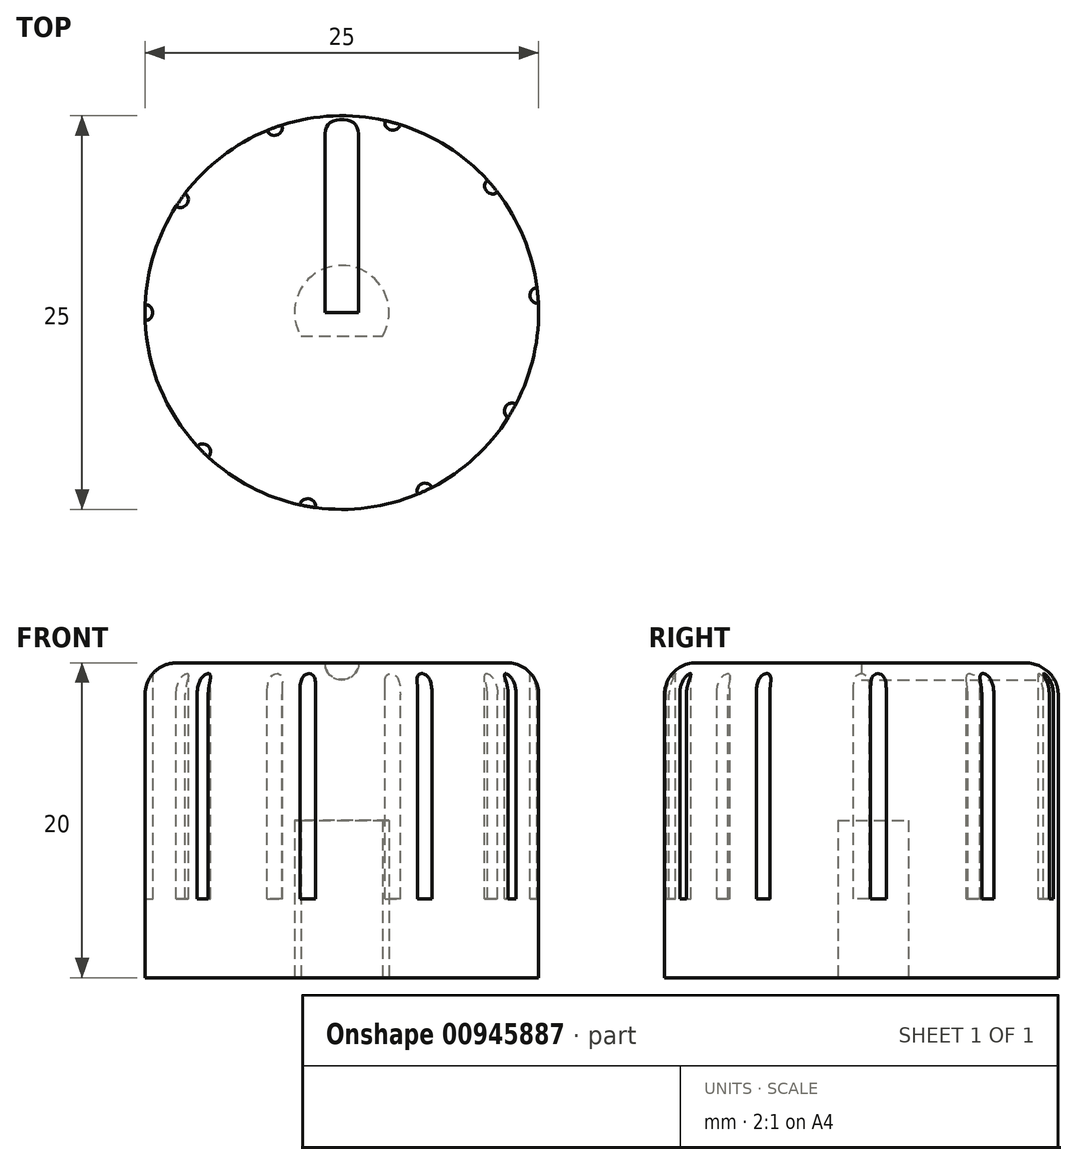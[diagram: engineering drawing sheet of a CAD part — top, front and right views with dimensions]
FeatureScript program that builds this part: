
annotation { "Feature Type Name" : "Feature", "Feature Type Description" : "" }
export const myFeature = defineFeature(function(context is Context, id is Id, definition is map)
    precondition{}
    {
        {
            var Q0;
            Q0=qCreatedBy(makeId("Top.planeOp"),FACE);
            var sketch = newSketch(context, id + "F0", { "sketchPlane" : qUnion([Q0])});
            skCircle(sketch, "E0", {"center": v(0, 0) * mm, "radius": 12.5 * mm});
            skCircle(sketch, "E1", {"center": v(0, 0) * mm, "radius": 3 * mm});
            skLineSegment(sketch, "E2", {"start": v(-2.6, -1.5) * mm, "end": v(2.6, -1.5) * mm});
            skSolve(sketch);
        }
        {
            var Q0;
            Q0=makeQuery(id+"F0.imprint","IMPRINT",FACE,{"disambiguationData":[TD([[makeQuery(id+"F0.imprint","IMPRINT",EDGE,{"derivedFrom":sQuery(id+"F0.wireOp",EDGE,"E0")}),1.0]])]});
            var Q1;
            {var subQ0=sQuery(id+"F0.wireOp",EDGE,"E2");Q1=makeQuery(id+"F0.imprint","IMPRINT",FACE,{"disambiguationData":[TD([[makeQuery(id+"F0.imprint","IMPRINT",EDGE,{"derivedFrom":subQ0}),-1.0]])]});}
            extrude(context, id + "F1", {"entities" : qUnion([Q0, Q1]), "depth" : 10 * mm, "offsetDistance" : 25 * mm});
        }
        {
            var Q0;
            Q0=makeQuery(id+"F1.opExtrude","CAP_FACE",FACE,{"disambiguationData":[OSD([sQuery(id+"F0.wireOp",EDGE,"E0"),sQuery(id+"F0.wireOp",EDGE,"E1"),sQuery(id+"F0.wireOp",EDGE,"E2")])],"isStart":false});
            var sketch = newSketch(context, id + "F2", { "sketchPlane" : qUnion([Q0])});
            skCircle(sketch, "E3", {"center": v(0, 0) * mm, "radius": 12.5 * mm});
            skSolve(sketch);
        }
        {
            var Q0;
            Q0=makeQuery(id+"F2.imprint","IMPRINT",FACE,{"disambiguationData":[TD([[makeQuery(id+"F2.imprint","IMPRINT",EDGE,{"derivedFrom":sQuery(id+"F2.wireOp",EDGE,"E3")}),1.0]])]});
            var Q1;
            Q1=makeQuery(id+"F2.imprint","IMPRINT",FACE,{"disambiguationData":[TD([[makeQuery(id+"F2.imprint","IMPRINT",EDGE,{"derivedFrom":makeQuery(id+"F1.opExtrude","CAP_EDGE",EDGE,{"disambiguationData":[OSD([sQuery(id+"F0.wireOp",EDGE,"E1")])],"isStart":false})}),1.0]])]});
            extrude(context, id + "F3", {"entities" : qUnion([Q0, Q1]), "operationType" : NewBodyOperationType.ADD, "depth" : 10 * mm, "offsetDistance" : 25 * mm});
        }
        {
            var Q0;
            Q0=makeQuery(id+"F3.opExtrude","CAP_FACE",FACE,{"disambiguationData":[OSD([sQuery(id+"F2.wireOp",EDGE,"E3")])],"isStart":false});
            var sketch = newSketch(context, id + "F4", { "sketchPlane" : qUnion([Q0])});
            skLineSegment(sketch, "E4", {"start": v(1.07, 0) * mm, "end": v(0, 0) * mm});
            skLineSegment(sketch, "E5", {"start": v(0, 0) * mm, "end": v(0, 12.81) * mm});
            skLineSegment(sketch, "E6", {"start": v(0, 12.81) * mm, "end": v(1.07, 12.81) * mm});
            skLineSegment(sketch, "E7", {"start": v(1.07, 12.81) * mm, "end": v(1.07, 0) * mm});
            skSolve(sketch);
        }
        {
            var Q0;
            {var subQ0=sQuery(id+"F4.wireOp",EDGE,"E4");Q0=makeQuery(id+"F4.imprint","IMPRINT",FACE,{"disambiguationData":[TD([[makeQuery(id+"F4.imprint","IMPRINT",EDGE,{"derivedFrom":subQ0}),-1.0]])]});}
            var Q1;
            {var subQ0=sQuery(id+"F4.wireOp",EDGE,"E6");Q1=makeQuery(id+"F4.imprint","IMPRINT",FACE,{"disambiguationData":[TD([[makeQuery(id+"F4.imprint","IMPRINT",EDGE,{"derivedFrom":subQ0}),-1.0]])]});}
            var Q2;
            Q2=sQuery(id+"F4.wireOp",EDGE,"E5");
            revolve(context, id + "F5", {"operationType" : NewBodyOperationType.REMOVE, "surfaceOperationType" : NewSurfaceOperationType.NEW, "entities" : qUnion([Q0, Q1]), "axis" : qUnion([Q2]), "revolveType" : RevolveType.FULL, "oppositeDirection" : true});
        }
        {
            var Q0;
            Q0=makeQuery(id+"F3.opExtrude","CAP_FACE",FACE,{"disambiguationData":[OSD([sQuery(id+"F2.wireOp",EDGE,"E3")])],"isStart":false});
            var sketch = newSketch(context, id + "F6", { "sketchPlane" : qUnion([Q0])});
            skLineSegment(sketch, "E8", {"start": v(0, 0) * mm, "end": v(-12.5, 0) * mm});
            skCircle(sketch, "E9", {"center": v(-12.5, 0) * mm, "radius": 0.5 * mm});
            skCircle(sketch, "E10.1.0", {"center": v(-10.24, 7.17) * mm, "radius": 0.5 * mm});
            skCircle(sketch, "E10.2.0", {"center": v(-4.28, 11.75) * mm, "radius": 0.5 * mm});
            skCircle(sketch, "E10.3.0", {"center": v(3.24, 12.07) * mm, "radius": 0.5 * mm});
            skCircle(sketch, "E10.4.0", {"center": v(9.58, 8.03) * mm, "radius": 0.5 * mm});
            skCircle(sketch, "E10.5.0", {"center": v(12.45, 1.09) * mm, "radius": 0.5 * mm});
            skCircle(sketch, "E10.6.0", {"center": v(10.83, -6.25) * mm, "radius": 0.5 * mm});
            skCircle(sketch, "E10.7.0", {"center": v(5.28, -11.33) * mm, "radius": 0.5 * mm});
            skCircle(sketch, "E10.8.0", {"center": v(-2.17, -12.31) * mm, "radius": 0.5 * mm});
            skCircle(sketch, "E10.9.0", {"center": v(-8.84, -8.84) * mm, "radius": 0.5 * mm});
            skPoint(sketch, "E10.center", {"position": v(0, 0) * mm});
            skLineSegment(sketch, "E10.anchor1", {"start": v(0, 0) * mm, "end": v(-12.5, 0) * mm, "construction": true});
            skLineSegment(sketch, "E10.anchor2", {"start": v(0, 0) * mm, "end": v(-8.84, -8.84) * mm, "construction": true});
            skSolve(sketch);
        }
        {
            var Q0;
            {var subQ0=sQuery(id+"F6.wireOp",EDGE,"E9");var subQ1=makeQuery(id+"F3.opExtrude","CAP_EDGE",EDGE,{"disambiguationData":[OSD([sQuery(id+"F2.wireOp",EDGE,"E3")])],"isStart":false});var subQ2=makeQuery(id+"F6.imprint","INTERSECT",VERTEX,{"disambiguationData":[OD(0.0)],"derivedFrom":[subQ1,subQ0]});Q0=makeQuery(id+"F6.imprint","IMPRINT",FACE,{"disambiguationData":[TD([[makeQuery(id+"F6.imprint","IMPRINT",EDGE,{"disambiguationData":[TD([[subQ2,1.0]])],"derivedFrom":subQ0}),1.0]])]});}
            var Q1;
            {var subQ0=sQuery(id+"F6.wireOp",EDGE,"E8");var subQ1=makeQuery(id+"F3.opExtrude","CAP_EDGE",EDGE,{"disambiguationData":[OSD([sQuery(id+"F2.wireOp",EDGE,"E3")])],"isStart":false});var subQ2=makeQuery(id+"F6.imprint","INTERSECT",VERTEX,{"derivedFrom":[subQ1,subQ0]});Q1=makeQuery(id+"F6.imprint","IMPRINT",FACE,{"disambiguationData":[TD([[makeQuery(id+"F6.imprint","IMPRINT",EDGE,{"disambiguationData":[TD([[subQ2,1.0]])],"derivedFrom":subQ0}),1.0]])]});}
            var Q2;
            {var subQ0=sQuery(id+"F6.wireOp",EDGE,"E8");var subQ1=makeQuery(id+"F3.opExtrude","CAP_EDGE",EDGE,{"disambiguationData":[OSD([sQuery(id+"F2.wireOp",EDGE,"E3")])],"isStart":false});var subQ2=makeQuery(id+"F6.imprint","INTERSECT",VERTEX,{"derivedFrom":[subQ1,subQ0]});Q2=makeQuery(id+"F6.imprint","IMPRINT",FACE,{"disambiguationData":[TD([[makeQuery(id+"F6.imprint","IMPRINT",EDGE,{"disambiguationData":[TD([[subQ2,1.0]])],"derivedFrom":subQ0}),-1.0]])]});}
            var Q3;
            {var subQ0=sQuery(id+"F6.wireOp",EDGE,"E10.1.0");var subQ1=makeQuery(id+"F3.opExtrude","CAP_EDGE",EDGE,{"disambiguationData":[OSD([sQuery(id+"F2.wireOp",EDGE,"E3")])],"isStart":false});var subQ2=makeQuery(id+"F6.imprint","INTERSECT",VERTEX,{"disambiguationData":[OD(0.0)],"derivedFrom":[subQ1,subQ0]});Q3=makeQuery(id+"F6.imprint","IMPRINT",FACE,{"disambiguationData":[TD([[makeQuery(id+"F6.imprint","IMPRINT",EDGE,{"disambiguationData":[TD([[subQ2,-1.0]])],"derivedFrom":subQ0}),1.0]])]});}
            var Q4;
            {var subQ0=sQuery(id+"F6.wireOp",EDGE,"E10.1.0");var subQ1=makeQuery(id+"F3.opExtrude","CAP_EDGE",EDGE,{"disambiguationData":[OSD([sQuery(id+"F2.wireOp",EDGE,"E3")])],"isStart":false});var subQ2=makeQuery(id+"F6.imprint","INTERSECT",VERTEX,{"disambiguationData":[OD(0.0)],"derivedFrom":[subQ1,subQ0]});Q4=makeQuery(id+"F6.imprint","IMPRINT",FACE,{"disambiguationData":[TD([[makeQuery(id+"F6.imprint","IMPRINT",EDGE,{"disambiguationData":[TD([[subQ2,1.0]])],"derivedFrom":subQ0}),1.0]])]});}
            var Q5;
            {var subQ0=sQuery(id+"F6.wireOp",EDGE,"E10.2.0");var subQ1=makeQuery(id+"F3.opExtrude","CAP_EDGE",EDGE,{"disambiguationData":[OSD([sQuery(id+"F2.wireOp",EDGE,"E3")])],"isStart":false});var subQ2=makeQuery(id+"F6.imprint","INTERSECT",VERTEX,{"disambiguationData":[OD(0.0)],"derivedFrom":[subQ1,subQ0]});Q5=makeQuery(id+"F6.imprint","IMPRINT",FACE,{"disambiguationData":[TD([[makeQuery(id+"F6.imprint","IMPRINT",EDGE,{"disambiguationData":[TD([[subQ2,1.0]])],"derivedFrom":subQ0}),1.0]])]});}
            var Q6;
            {var subQ0=sQuery(id+"F6.wireOp",EDGE,"E10.2.0");var subQ1=makeQuery(id+"F3.opExtrude","CAP_EDGE",EDGE,{"disambiguationData":[OSD([sQuery(id+"F2.wireOp",EDGE,"E3")])],"isStart":false});var subQ2=makeQuery(id+"F6.imprint","INTERSECT",VERTEX,{"disambiguationData":[OD(0.0)],"derivedFrom":[subQ1,subQ0]});Q6=makeQuery(id+"F6.imprint","IMPRINT",FACE,{"disambiguationData":[TD([[makeQuery(id+"F6.imprint","IMPRINT",EDGE,{"disambiguationData":[TD([[subQ2,-1.0]])],"derivedFrom":subQ0}),1.0]])]});}
            var Q7;
            {var subQ0=sQuery(id+"F6.wireOp",EDGE,"E10.3.0");var subQ1=makeQuery(id+"F3.opExtrude","CAP_EDGE",EDGE,{"disambiguationData":[OSD([sQuery(id+"F2.wireOp",EDGE,"E3")])],"isStart":false});var subQ2=makeQuery(id+"F6.imprint","INTERSECT",VERTEX,{"disambiguationData":[OD(0.0)],"derivedFrom":[subQ1,subQ0]});Q7=makeQuery(id+"F6.imprint","IMPRINT",FACE,{"disambiguationData":[TD([[makeQuery(id+"F6.imprint","IMPRINT",EDGE,{"disambiguationData":[TD([[subQ2,1.0]])],"derivedFrom":subQ0}),1.0]])]});}
            var Q8;
            {var subQ0=sQuery(id+"F6.wireOp",EDGE,"E10.4.0");var subQ1=makeQuery(id+"F3.opExtrude","CAP_EDGE",EDGE,{"disambiguationData":[OSD([sQuery(id+"F2.wireOp",EDGE,"E3")])],"isStart":false});var subQ2=makeQuery(id+"F6.imprint","INTERSECT",VERTEX,{"disambiguationData":[OD(0.0)],"derivedFrom":[subQ1,subQ0]});Q8=makeQuery(id+"F6.imprint","IMPRINT",FACE,{"disambiguationData":[TD([[makeQuery(id+"F6.imprint","IMPRINT",EDGE,{"disambiguationData":[TD([[subQ2,1.0]])],"derivedFrom":subQ0}),1.0]])]});}
            var Q9;
            {var subQ0=sQuery(id+"F6.wireOp",EDGE,"E10.4.0");var subQ1=makeQuery(id+"F3.opExtrude","CAP_EDGE",EDGE,{"disambiguationData":[OSD([sQuery(id+"F2.wireOp",EDGE,"E3")])],"isStart":false});var subQ2=makeQuery(id+"F6.imprint","INTERSECT",VERTEX,{"disambiguationData":[OD(0.0)],"derivedFrom":[subQ1,subQ0]});Q9=makeQuery(id+"F6.imprint","IMPRINT",FACE,{"disambiguationData":[TD([[makeQuery(id+"F6.imprint","IMPRINT",EDGE,{"disambiguationData":[TD([[subQ2,-1.0]])],"derivedFrom":subQ0}),1.0]])]});}
            var Q10;
            {var subQ0=sQuery(id+"F6.wireOp",EDGE,"E10.5.0");var subQ1=makeQuery(id+"F3.opExtrude","CAP_EDGE",EDGE,{"disambiguationData":[OSD([sQuery(id+"F2.wireOp",EDGE,"E3")])],"isStart":false});var subQ2=makeQuery(id+"F6.imprint","INTERSECT",VERTEX,{"disambiguationData":[OD(0.0)],"derivedFrom":[subQ1,subQ0]});Q10=makeQuery(id+"F6.imprint","IMPRINT",FACE,{"disambiguationData":[TD([[makeQuery(id+"F6.imprint","IMPRINT",EDGE,{"disambiguationData":[TD([[subQ2,1.0]])],"derivedFrom":subQ0}),1.0]])]});}
            var Q11;
            {var subQ0=sQuery(id+"F6.wireOp",EDGE,"E10.5.0");var subQ1=makeQuery(id+"F3.opExtrude","CAP_EDGE",EDGE,{"disambiguationData":[OSD([sQuery(id+"F2.wireOp",EDGE,"E3")])],"isStart":false});var subQ2=makeQuery(id+"F6.imprint","INTERSECT",VERTEX,{"disambiguationData":[OD(0.0)],"derivedFrom":[subQ1,subQ0]});Q11=makeQuery(id+"F6.imprint","IMPRINT",FACE,{"disambiguationData":[TD([[makeQuery(id+"F6.imprint","IMPRINT",EDGE,{"disambiguationData":[TD([[subQ2,-1.0]])],"derivedFrom":subQ0}),1.0]])]});}
            var Q12;
            {var subQ0=sQuery(id+"F6.wireOp",EDGE,"E10.6.0");var subQ1=makeQuery(id+"F3.opExtrude","CAP_EDGE",EDGE,{"disambiguationData":[OSD([sQuery(id+"F2.wireOp",EDGE,"E3")])],"isStart":false});var subQ2=makeQuery(id+"F6.imprint","INTERSECT",VERTEX,{"disambiguationData":[OD(0.0)],"derivedFrom":[subQ1,subQ0]});Q12=makeQuery(id+"F6.imprint","IMPRINT",FACE,{"disambiguationData":[TD([[makeQuery(id+"F6.imprint","IMPRINT",EDGE,{"disambiguationData":[TD([[subQ2,1.0]])],"derivedFrom":subQ0}),1.0]])]});}
            var Q13;
            {var subQ0=sQuery(id+"F6.wireOp",EDGE,"E10.6.0");var subQ1=makeQuery(id+"F3.opExtrude","CAP_EDGE",EDGE,{"disambiguationData":[OSD([sQuery(id+"F2.wireOp",EDGE,"E3")])],"isStart":false});var subQ2=makeQuery(id+"F6.imprint","INTERSECT",VERTEX,{"disambiguationData":[OD(0.0)],"derivedFrom":[subQ1,subQ0]});Q13=makeQuery(id+"F6.imprint","IMPRINT",FACE,{"disambiguationData":[TD([[makeQuery(id+"F6.imprint","IMPRINT",EDGE,{"disambiguationData":[TD([[subQ2,-1.0]])],"derivedFrom":subQ0}),1.0]])]});}
            var Q14;
            {var subQ0=sQuery(id+"F6.wireOp",EDGE,"E10.7.0");var subQ1=makeQuery(id+"F3.opExtrude","CAP_EDGE",EDGE,{"disambiguationData":[OSD([sQuery(id+"F2.wireOp",EDGE,"E3")])],"isStart":false});var subQ2=makeQuery(id+"F6.imprint","INTERSECT",VERTEX,{"disambiguationData":[OD(0.0)],"derivedFrom":[subQ1,subQ0]});Q14=makeQuery(id+"F6.imprint","IMPRINT",FACE,{"disambiguationData":[TD([[makeQuery(id+"F6.imprint","IMPRINT",EDGE,{"disambiguationData":[TD([[subQ2,1.0]])],"derivedFrom":subQ0}),1.0]])]});}
            var Q15;
            {var subQ0=sQuery(id+"F6.wireOp",EDGE,"E10.7.0");var subQ1=makeQuery(id+"F3.opExtrude","CAP_EDGE",EDGE,{"disambiguationData":[OSD([sQuery(id+"F2.wireOp",EDGE,"E3")])],"isStart":false});var subQ2=makeQuery(id+"F6.imprint","INTERSECT",VERTEX,{"disambiguationData":[OD(0.0)],"derivedFrom":[subQ1,subQ0]});Q15=makeQuery(id+"F6.imprint","IMPRINT",FACE,{"disambiguationData":[TD([[makeQuery(id+"F6.imprint","IMPRINT",EDGE,{"disambiguationData":[TD([[subQ2,-1.0]])],"derivedFrom":subQ0}),1.0]])]});}
            var Q16;
            {var subQ0=sQuery(id+"F6.wireOp",EDGE,"E10.8.0");var subQ1=makeQuery(id+"F3.opExtrude","CAP_EDGE",EDGE,{"disambiguationData":[OSD([sQuery(id+"F2.wireOp",EDGE,"E3")])],"isStart":false});var subQ2=makeQuery(id+"F6.imprint","INTERSECT",VERTEX,{"disambiguationData":[OD(0.0)],"derivedFrom":[subQ1,subQ0]});Q16=makeQuery(id+"F6.imprint","IMPRINT",FACE,{"disambiguationData":[TD([[makeQuery(id+"F6.imprint","IMPRINT",EDGE,{"disambiguationData":[TD([[subQ2,1.0]])],"derivedFrom":subQ0}),1.0]])]});}
            var Q17;
            {var subQ0=sQuery(id+"F6.wireOp",EDGE,"E10.8.0");var subQ1=makeQuery(id+"F3.opExtrude","CAP_EDGE",EDGE,{"disambiguationData":[OSD([sQuery(id+"F2.wireOp",EDGE,"E3")])],"isStart":false});var subQ2=makeQuery(id+"F6.imprint","INTERSECT",VERTEX,{"disambiguationData":[OD(0.0)],"derivedFrom":[subQ1,subQ0]});Q17=makeQuery(id+"F6.imprint","IMPRINT",FACE,{"disambiguationData":[TD([[makeQuery(id+"F6.imprint","IMPRINT",EDGE,{"disambiguationData":[TD([[subQ2,-1.0]])],"derivedFrom":subQ0}),1.0]])]});}
            var Q18;
            {var subQ0=sQuery(id+"F6.wireOp",EDGE,"E10.9.0");var subQ1=makeQuery(id+"F3.opExtrude","CAP_EDGE",EDGE,{"disambiguationData":[OSD([sQuery(id+"F2.wireOp",EDGE,"E3")])],"isStart":false});var subQ2=makeQuery(id+"F6.imprint","INTERSECT",VERTEX,{"disambiguationData":[OD(0.0)],"derivedFrom":[subQ1,subQ0]});Q18=makeQuery(id+"F6.imprint","IMPRINT",FACE,{"disambiguationData":[TD([[makeQuery(id+"F6.imprint","IMPRINT",EDGE,{"disambiguationData":[TD([[subQ2,1.0]])],"derivedFrom":subQ0}),1.0]])]});}
            var Q19;
            {var subQ0=sQuery(id+"F6.wireOp",EDGE,"E10.9.0");var subQ1=makeQuery(id+"F3.opExtrude","CAP_EDGE",EDGE,{"disambiguationData":[OSD([sQuery(id+"F2.wireOp",EDGE,"E3")])],"isStart":false});var subQ2=makeQuery(id+"F6.imprint","INTERSECT",VERTEX,{"disambiguationData":[OD(0.0)],"derivedFrom":[subQ1,subQ0]});Q19=makeQuery(id+"F6.imprint","IMPRINT",FACE,{"disambiguationData":[TD([[makeQuery(id+"F6.imprint","IMPRINT",EDGE,{"disambiguationData":[TD([[subQ2,-1.0]])],"derivedFrom":subQ0}),1.0]])]});}
            var Q20;
            {var subQ0=sQuery(id+"F6.wireOp",EDGE,"E10.3.0");var subQ1=makeQuery(id+"F3.opExtrude","CAP_EDGE",EDGE,{"disambiguationData":[OSD([sQuery(id+"F2.wireOp",EDGE,"E3")])],"isStart":false});var subQ2=makeQuery(id+"F6.imprint","INTERSECT",VERTEX,{"disambiguationData":[OD(0.0)],"derivedFrom":[subQ1,subQ0]});Q20=makeQuery(id+"F6.imprint","IMPRINT",FACE,{"disambiguationData":[TD([[makeQuery(id+"F6.imprint","IMPRINT",EDGE,{"disambiguationData":[TD([[subQ2,-1.0]])],"derivedFrom":subQ0}),1.0]])]});}
            extrude(context, id + "F7", {"entities" : qUnion([Q0, Q1, Q2, Q3, Q4, Q5, Q6, Q7, Q8, Q9, Q10, Q11, Q12, Q13, Q14, Q15, Q16, Q17, Q18, Q19, Q20]), "operationType" : NewBodyOperationType.REMOVE, "oppositeDirection" : true, "depth" : 15 * mm, "offsetDistance" : 25 * mm});
        }
        {
            var Q0;
            {var subQ0=sQuery(id+"F2.wireOp",EDGE,"E3");Q0=makeQuery(id+"F7.boolean.opBoolean","SPLIT",EDGE,{"disambiguationData":[TD([makeQuery(id+"F1.opExtrude","SWEPT_FACE",FACE,{"disambiguationData":[OSD([sQuery(id+"F0.wireOp",EDGE,"E0")])]}),makeQuery(id+"F3.opExtrude","SWEPT_FACE",FACE,{"disambiguationData":[OSD([subQ0])]}),makeQuery(id+"F3.opExtrude","CAP_FACE",FACE,{"disambiguationData":[OSD([subQ0])],"isStart":false}),makeQuery(id+"F7.opExtrude","SWEPT_FACE",FACE,{"disambiguationData":[OSD([sQuery(id+"F6.wireOp",EDGE,"E10.1.0")])]}),makeQuery(id+"F7.opExtrude","SWEPT_FACE",FACE,{"disambiguationData":[OSD([sQuery(id+"F6.wireOp",EDGE,"E10.2.0")])]})])],"derivedFrom":makeQuery(id+"F3.opExtrude","CAP_EDGE",EDGE,{"disambiguationData":[OSD([subQ0])],"isStart":false})});}
            var Q1;
            {var subQ0=sQuery(id+"F2.wireOp",EDGE,"E3");Q1=makeQuery(id+"F7.boolean.opBoolean","SPLIT",EDGE,{"disambiguationData":[TD([makeQuery(id+"F1.opExtrude","SWEPT_FACE",FACE,{"disambiguationData":[OSD([sQuery(id+"F0.wireOp",EDGE,"E0")])]}),makeQuery(id+"F3.opExtrude","SWEPT_FACE",FACE,{"disambiguationData":[OSD([subQ0])]}),makeQuery(id+"F3.opExtrude","CAP_FACE",FACE,{"disambiguationData":[OSD([subQ0])],"isStart":false}),makeQuery(id+"F5.boolean.opBoolean","COPY",FACE,{"derivedFrom":makeQuery(id+"F5.opRevolve","SWEPT_FACE",FACE,{"disambiguationData":[OSD([sQuery(id+"F4.wireOp",EDGE,"E7")])]})}),makeQuery(id+"F7.opExtrude","SWEPT_FACE",FACE,{"disambiguationData":[OSD([sQuery(id+"F6.wireOp",EDGE,"E10.2.0")])]})])],"derivedFrom":makeQuery(id+"F3.opExtrude","CAP_EDGE",EDGE,{"disambiguationData":[OSD([subQ0])],"isStart":false})});}
            var Q2;
            {var subQ0=sQuery(id+"F2.wireOp",EDGE,"E3");Q2=makeQuery(id+"F7.boolean.opBoolean","SPLIT",EDGE,{"disambiguationData":[TD([makeQuery(id+"F1.opExtrude","SWEPT_FACE",FACE,{"disambiguationData":[OSD([sQuery(id+"F0.wireOp",EDGE,"E0")])]}),makeQuery(id+"F3.opExtrude","SWEPT_FACE",FACE,{"disambiguationData":[OSD([subQ0])]}),makeQuery(id+"F3.opExtrude","CAP_FACE",FACE,{"disambiguationData":[OSD([subQ0])],"isStart":false}),makeQuery(id+"F5.boolean.opBoolean","COPY",FACE,{"derivedFrom":makeQuery(id+"F5.opRevolve","SWEPT_FACE",FACE,{"disambiguationData":[OSD([sQuery(id+"F4.wireOp",EDGE,"E7")])]})}),makeQuery(id+"F7.opExtrude","SWEPT_FACE",FACE,{"disambiguationData":[OSD([sQuery(id+"F6.wireOp",EDGE,"E10.3.0")])]})])],"derivedFrom":makeQuery(id+"F3.opExtrude","CAP_EDGE",EDGE,{"disambiguationData":[OSD([subQ0])],"isStart":false})});}
            var Q3;
            {var subQ0=sQuery(id+"F2.wireOp",EDGE,"E3");Q3=makeQuery(id+"F7.boolean.opBoolean","SPLIT",EDGE,{"disambiguationData":[TD([makeQuery(id+"F1.opExtrude","SWEPT_FACE",FACE,{"disambiguationData":[OSD([sQuery(id+"F0.wireOp",EDGE,"E0")])]}),makeQuery(id+"F3.opExtrude","SWEPT_FACE",FACE,{"disambiguationData":[OSD([subQ0])]}),makeQuery(id+"F3.opExtrude","CAP_FACE",FACE,{"disambiguationData":[OSD([subQ0])],"isStart":false}),makeQuery(id+"F7.opExtrude","SWEPT_FACE",FACE,{"disambiguationData":[OSD([sQuery(id+"F6.wireOp",EDGE,"E10.3.0")])]}),makeQuery(id+"F7.opExtrude","SWEPT_FACE",FACE,{"disambiguationData":[OSD([sQuery(id+"F6.wireOp",EDGE,"E10.4.0")])]})])],"derivedFrom":makeQuery(id+"F3.opExtrude","CAP_EDGE",EDGE,{"disambiguationData":[OSD([subQ0])],"isStart":false})});}
            var Q4;
            {var subQ0=sQuery(id+"F2.wireOp",EDGE,"E3");Q4=makeQuery(id+"F7.boolean.opBoolean","SPLIT",EDGE,{"disambiguationData":[TD([makeQuery(id+"F1.opExtrude","SWEPT_FACE",FACE,{"disambiguationData":[OSD([sQuery(id+"F0.wireOp",EDGE,"E0")])]}),makeQuery(id+"F3.opExtrude","SWEPT_FACE",FACE,{"disambiguationData":[OSD([subQ0])]}),makeQuery(id+"F3.opExtrude","CAP_FACE",FACE,{"disambiguationData":[OSD([subQ0])],"isStart":false}),makeQuery(id+"F7.opExtrude","SWEPT_FACE",FACE,{"disambiguationData":[OSD([sQuery(id+"F6.wireOp",EDGE,"E10.4.0")])]}),makeQuery(id+"F7.opExtrude","SWEPT_FACE",FACE,{"disambiguationData":[OSD([sQuery(id+"F6.wireOp",EDGE,"E10.5.0")])]})])],"derivedFrom":makeQuery(id+"F3.opExtrude","CAP_EDGE",EDGE,{"disambiguationData":[OSD([subQ0])],"isStart":false})});}
            var Q5;
            {var subQ0=sQuery(id+"F2.wireOp",EDGE,"E3");Q5=makeQuery(id+"F7.boolean.opBoolean","SPLIT",EDGE,{"disambiguationData":[TD([makeQuery(id+"F1.opExtrude","SWEPT_FACE",FACE,{"disambiguationData":[OSD([sQuery(id+"F0.wireOp",EDGE,"E0")])]}),makeQuery(id+"F3.opExtrude","SWEPT_FACE",FACE,{"disambiguationData":[OSD([subQ0])]}),makeQuery(id+"F3.opExtrude","CAP_FACE",FACE,{"disambiguationData":[OSD([subQ0])],"isStart":false}),makeQuery(id+"F7.opExtrude","SWEPT_FACE",FACE,{"disambiguationData":[OSD([sQuery(id+"F6.wireOp",EDGE,"E9"),dummyQuery(id+"F6.imprint",EDGE)])]}),makeQuery(id+"F7.opExtrude","SWEPT_FACE",FACE,{"disambiguationData":[OSD([sQuery(id+"F6.wireOp",EDGE,"E10.1.0")])]})])],"derivedFrom":makeQuery(id+"F3.opExtrude","CAP_EDGE",EDGE,{"disambiguationData":[OSD([subQ0])],"isStart":false})});}
            var Q6;
            {var subQ0=sQuery(id+"F2.wireOp",EDGE,"E3");Q6=makeQuery(id+"F7.boolean.opBoolean","SPLIT",EDGE,{"disambiguationData":[TD([makeQuery(id+"F1.opExtrude","SWEPT_FACE",FACE,{"disambiguationData":[OSD([sQuery(id+"F0.wireOp",EDGE,"E0")])]}),makeQuery(id+"F3.opExtrude","SWEPT_FACE",FACE,{"disambiguationData":[OSD([subQ0])]}),makeQuery(id+"F3.opExtrude","CAP_FACE",FACE,{"disambiguationData":[OSD([subQ0])],"isStart":false}),makeQuery(id+"F7.opExtrude","SWEPT_FACE",FACE,{"disambiguationData":[OSD([sQuery(id+"F6.wireOp",EDGE,"E9"),dummyQuery(id+"F6.imprint",EDGE)])]}),makeQuery(id+"F7.opExtrude","SWEPT_FACE",FACE,{"disambiguationData":[OSD([sQuery(id+"F6.wireOp",EDGE,"E10.9.0")])]})])],"derivedFrom":makeQuery(id+"F3.opExtrude","CAP_EDGE",EDGE,{"disambiguationData":[OSD([subQ0])],"isStart":false})});}
            var Q7;
            {var subQ0=sQuery(id+"F2.wireOp",EDGE,"E3");Q7=makeQuery(id+"F7.boolean.opBoolean","SPLIT",EDGE,{"disambiguationData":[TD([makeQuery(id+"F1.opExtrude","SWEPT_FACE",FACE,{"disambiguationData":[OSD([sQuery(id+"F0.wireOp",EDGE,"E0")])]}),makeQuery(id+"F3.opExtrude","SWEPT_FACE",FACE,{"disambiguationData":[OSD([subQ0])]}),makeQuery(id+"F3.opExtrude","CAP_FACE",FACE,{"disambiguationData":[OSD([subQ0])],"isStart":false}),makeQuery(id+"F7.opExtrude","SWEPT_FACE",FACE,{"disambiguationData":[OSD([sQuery(id+"F6.wireOp",EDGE,"E10.8.0")])]}),makeQuery(id+"F7.opExtrude","SWEPT_FACE",FACE,{"disambiguationData":[OSD([sQuery(id+"F6.wireOp",EDGE,"E10.9.0")])]})])],"derivedFrom":makeQuery(id+"F3.opExtrude","CAP_EDGE",EDGE,{"disambiguationData":[OSD([subQ0])],"isStart":false})});}
            var Q8;
            {var subQ0=sQuery(id+"F2.wireOp",EDGE,"E3");Q8=makeQuery(id+"F7.boolean.opBoolean","SPLIT",EDGE,{"disambiguationData":[TD([makeQuery(id+"F1.opExtrude","SWEPT_FACE",FACE,{"disambiguationData":[OSD([sQuery(id+"F0.wireOp",EDGE,"E0")])]}),makeQuery(id+"F3.opExtrude","SWEPT_FACE",FACE,{"disambiguationData":[OSD([subQ0])]}),makeQuery(id+"F3.opExtrude","CAP_FACE",FACE,{"disambiguationData":[OSD([subQ0])],"isStart":false}),makeQuery(id+"F7.opExtrude","SWEPT_FACE",FACE,{"disambiguationData":[OSD([sQuery(id+"F6.wireOp",EDGE,"E10.7.0")])]}),makeQuery(id+"F7.opExtrude","SWEPT_FACE",FACE,{"disambiguationData":[OSD([sQuery(id+"F6.wireOp",EDGE,"E10.8.0")])]})])],"derivedFrom":makeQuery(id+"F3.opExtrude","CAP_EDGE",EDGE,{"disambiguationData":[OSD([subQ0])],"isStart":false})});}
            var Q9;
            {var subQ0=sQuery(id+"F2.wireOp",EDGE,"E3");Q9=makeQuery(id+"F7.boolean.opBoolean","SPLIT",EDGE,{"disambiguationData":[TD([makeQuery(id+"F1.opExtrude","SWEPT_FACE",FACE,{"disambiguationData":[OSD([sQuery(id+"F0.wireOp",EDGE,"E0")])]}),makeQuery(id+"F3.opExtrude","SWEPT_FACE",FACE,{"disambiguationData":[OSD([subQ0])]}),makeQuery(id+"F3.opExtrude","CAP_FACE",FACE,{"disambiguationData":[OSD([subQ0])],"isStart":false}),makeQuery(id+"F7.opExtrude","SWEPT_FACE",FACE,{"disambiguationData":[OSD([sQuery(id+"F6.wireOp",EDGE,"E10.6.0")])]}),makeQuery(id+"F7.opExtrude","SWEPT_FACE",FACE,{"disambiguationData":[OSD([sQuery(id+"F6.wireOp",EDGE,"E10.7.0")])]})])],"derivedFrom":makeQuery(id+"F3.opExtrude","CAP_EDGE",EDGE,{"disambiguationData":[OSD([subQ0])],"isStart":false})});}
            var Q10;
            {var subQ0=sQuery(id+"F2.wireOp",EDGE,"E3");Q10=makeQuery(id+"F7.boolean.opBoolean","SPLIT",EDGE,{"disambiguationData":[TD([makeQuery(id+"F1.opExtrude","SWEPT_FACE",FACE,{"disambiguationData":[OSD([sQuery(id+"F0.wireOp",EDGE,"E0")])]}),makeQuery(id+"F3.opExtrude","SWEPT_FACE",FACE,{"disambiguationData":[OSD([subQ0])]}),makeQuery(id+"F3.opExtrude","CAP_FACE",FACE,{"disambiguationData":[OSD([subQ0])],"isStart":false}),makeQuery(id+"F7.opExtrude","SWEPT_FACE",FACE,{"disambiguationData":[OSD([sQuery(id+"F6.wireOp",EDGE,"E10.5.0")])]}),makeQuery(id+"F7.opExtrude","SWEPT_FACE",FACE,{"disambiguationData":[OSD([sQuery(id+"F6.wireOp",EDGE,"E10.6.0")])]})])],"derivedFrom":makeQuery(id+"F3.opExtrude","CAP_EDGE",EDGE,{"disambiguationData":[OSD([subQ0])],"isStart":false})});}
            fillet(context, id + "F8", {"entities" : qUnion([Q0, Q1, Q2, Q3, Q4, Q5, Q6, Q7, Q8, Q9, Q10]), "radius" : 2 * mm, "tangentPropagation" : true, "allowEdgeOverflow" : false});
        }
        {
            var Q0;
            {var subQ0=sQuery(id+"F6.wireOp",EDGE,"E10.9.0");var subQ1=makeQuery(id+"F3.opExtrude","CAP_EDGE",EDGE,{"disambiguationData":[OSD([sQuery(id+"F2.wireOp",EDGE,"E3")])],"isStart":false});var subQ2=makeQuery(id+"F6.imprint","INTERSECT",VERTEX,{"disambiguationData":[OD(0.0)],"derivedFrom":[subQ1,subQ0]});Q0=makeQuery(id+"F6.imprint","IMPRINT",FACE,{"disambiguationData":[TD([[makeQuery(id+"F6.imprint","IMPRINT",EDGE,{"disambiguationData":[TD([[subQ2,-1.0]])],"derivedFrom":subQ0}),1.0]])]});}
            var Q1;
            {var subQ0=sQuery(id+"F6.wireOp",EDGE,"E10.9.0");var subQ1=makeQuery(id+"F3.opExtrude","CAP_EDGE",EDGE,{"disambiguationData":[OSD([sQuery(id+"F2.wireOp",EDGE,"E3")])],"isStart":false});var subQ2=makeQuery(id+"F6.imprint","INTERSECT",VERTEX,{"disambiguationData":[OD(0.0)],"derivedFrom":[subQ1,subQ0]});Q1=makeQuery(id+"F6.imprint","IMPRINT",FACE,{"disambiguationData":[TD([[makeQuery(id+"F6.imprint","IMPRINT",EDGE,{"disambiguationData":[TD([[subQ2,1.0]])],"derivedFrom":subQ0}),1.0]])]});}
            var Q2;
            {var subQ0=sQuery(id+"F6.wireOp",EDGE,"E10.8.0");var subQ1=makeQuery(id+"F3.opExtrude","CAP_EDGE",EDGE,{"disambiguationData":[OSD([sQuery(id+"F2.wireOp",EDGE,"E3")])],"isStart":false});var subQ2=makeQuery(id+"F6.imprint","INTERSECT",VERTEX,{"disambiguationData":[OD(0.0)],"derivedFrom":[subQ1,subQ0]});Q2=makeQuery(id+"F6.imprint","IMPRINT",FACE,{"disambiguationData":[TD([[makeQuery(id+"F6.imprint","IMPRINT",EDGE,{"disambiguationData":[TD([[subQ2,-1.0]])],"derivedFrom":subQ0}),1.0]])]});}
            var Q3;
            Q3=sQuery(id+"F6.wireOp",EDGE,"E9");
            var Q4;
            Q4=sQuery(id+"F6.wireOp",EDGE,"E10.1.0");
            var Q5;
            Q5=sQuery(id+"F6.wireOp",EDGE,"E10.2.0");
            var Q6;
            Q6=sQuery(id+"F6.wireOp",EDGE,"E10.3.0");
            var Q7;
            Q7=sQuery(id+"F6.wireOp",EDGE,"E10.4.0");
            var Q8;
            Q8=sQuery(id+"F6.wireOp",EDGE,"E10.5.0");
            var Q9;
            Q9=sQuery(id+"F6.wireOp",EDGE,"E10.6.0");
            var Q10;
            Q10=sQuery(id+"F6.wireOp",EDGE,"E10.7.0");
            var Q11;
            Q11=sQuery(id+"F6.wireOp",EDGE,"E10.8.0");
            var Q12;
            Q12=sQuery(id+"F6.wireOp",EDGE,"E10.9.0");
            extrude(context, id + "F9", {"entities" : qUnion([Q0, Q1, Q2]), "operationType" : NewBodyOperationType.REMOVE, "surfaceEntities" : qUnion([Q3, Q4, Q5, Q6, Q7, Q8, Q9, Q10, Q11, Q12]), "oppositeDirection" : true, "depth" : 15 * mm, "offsetDistance" : 25 * mm});
        }
    });
